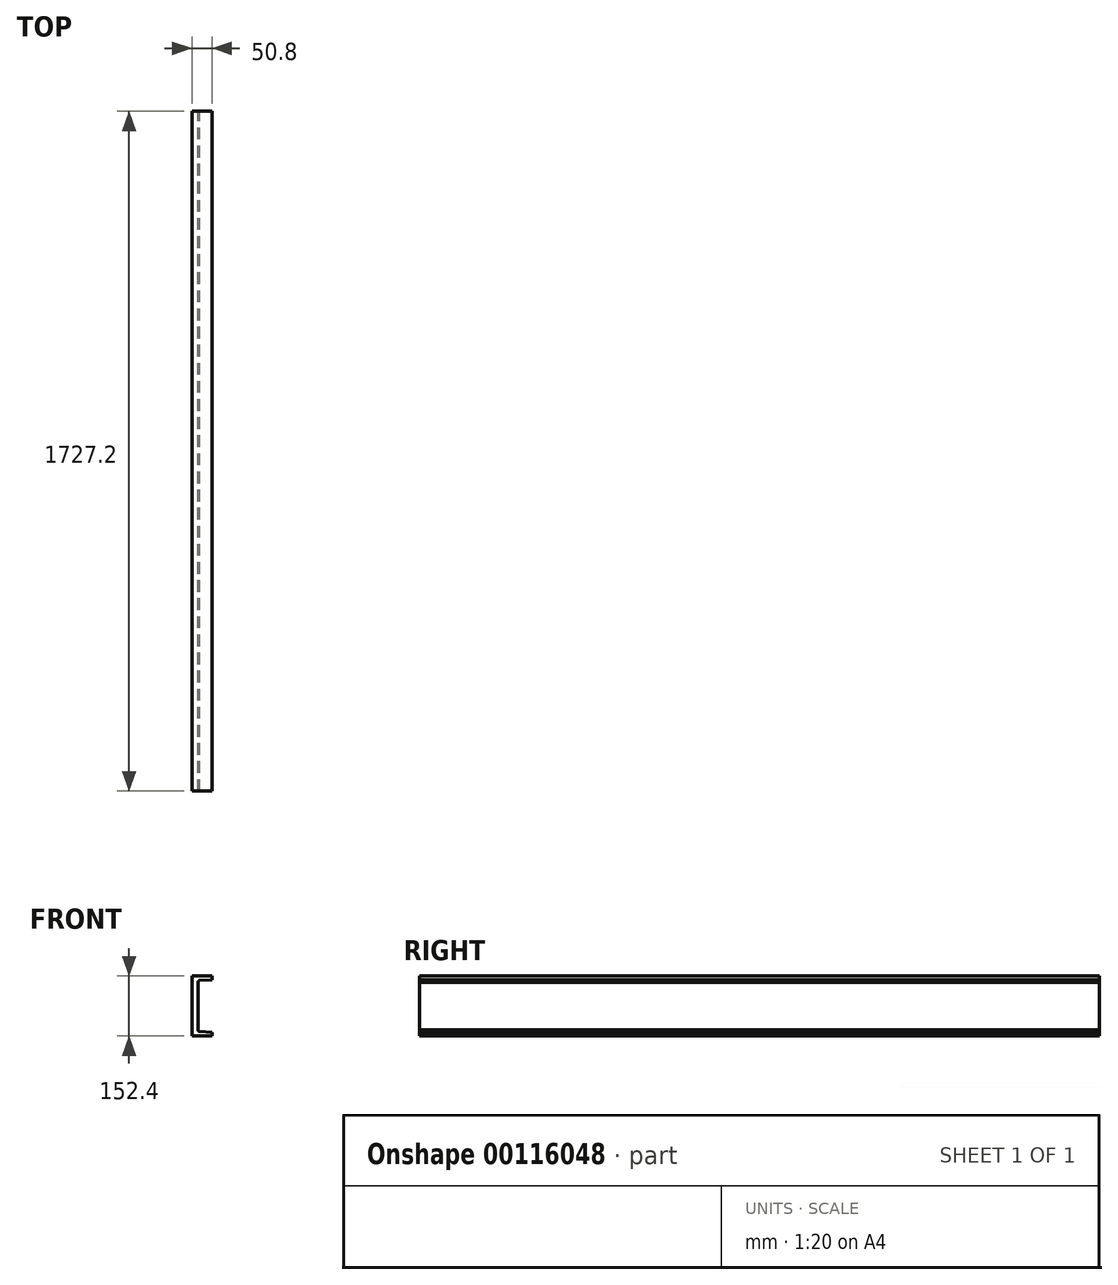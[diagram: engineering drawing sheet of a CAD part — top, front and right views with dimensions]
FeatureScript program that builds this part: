
annotation { "Feature Type Name" : "Feature", "Feature Type Description" : "" }
export const myFeature = defineFeature(function(context is Context, id is Id, definition is map)
    precondition{}
    {
        {
            var Q0;
            Q0=qCreatedBy(makeId("Front.planeOp"),FACE);
            var sketch = newSketch(context, id + "F0", { "sketchPlane" : qUnion([Q0])});
            skLineSegment(sketch, "E0", {"start": v(0, 0) * mm, "end": v(0, 152.4) * mm});
            skLineSegment(sketch, "E1", {"start": v(0, 152.4) * mm, "end": v(50.8, 152.4) * mm});
            skLineSegment(sketch, "E2", {"start": v(50.8, 152.4) * mm, "end": v(50.8, 142.88) * mm});
            skArc(sketch, "E3", {"start": v(19.71, 140.97) * mm, "mid": v(16.73, 139.6) * mm, "end": v(15.68, 136.48) * mm});
            skLineSegment(sketch, "E4", {"start": v(19.71, 140.97) * mm, "end": v(50.8, 142.88) * mm});
            skLineSegment(sketch, "E5", {"start": v(15.68, 136.48) * mm, "end": v(15.68, 76.2) * mm});
            skLineSegment(sketch, "E6.MirrorCS", {"start": v(0, 152.4) * mm, "end": v(0, 0) * mm});
            skLineSegment(sketch, "E7.MirrorCS", {"start": v(0, 0) * mm, "end": v(50.8, 0) * mm});
            skLineSegment(sketch, "E8.MirrorCS", {"start": v(50.8, 0) * mm, "end": v(50.8, 9.53) * mm});
            skLineSegment(sketch, "E9.MirrorCS", {"start": v(19.71, 11.43) * mm, "end": v(50.8, 9.53) * mm});
            skLineSegment(sketch, "E10.MirrorCS", {"start": v(15.68, 15.92) * mm, "end": v(15.68, 76.2) * mm});
            skArc(sketch, "E11.MirrorCS", {"start": v(19.71, 11.43) * mm, "mid": v(16.73, 12.8) * mm, "end": v(15.68, 15.92) * mm});
            skSolve(sketch);
        }
        {
            var Q0;
            Q0=makeQuery(id+"F0.imprint","IMPRINT",FACE,{"disambiguationData":[TD([[makeQuery(id+"F0.imprint","IMPRINT",EDGE,{"derivedFrom":sQuery(id+"F0.wireOp",EDGE,"E1")}),-1.0]])]});
            extrude(context, id + "F1", {"entities" : qUnion([Q0]), "depth" : 1727.2 * mm});
        }
    });
